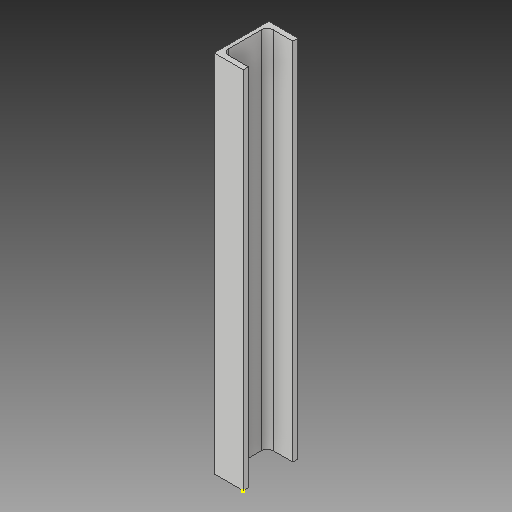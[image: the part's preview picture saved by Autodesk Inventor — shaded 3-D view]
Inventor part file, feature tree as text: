
AUTODESK INVENTOR PART (.ipt)
format: ipt  version: 2019 (Build 230136000, 136)  size: 93,184 bytes
history: native  units: in
note: dims shown in document units (in); Inventor stores cm internally (conversion verified against a paired STEP export)
features: other x3, sketch x2
ambient origin geometry x8: Origin, YZ Plane, XZ Plane, XY Plane, X Axis, Y Axis, Z Axis, Center Point
bodies: Solid1 (feature_tree)
feature tree (5):
  other  "Channel2_MIR1.ipt"
  other  "Solid1::Channel2_MIR1.ipt"
  other  "TaggingFeature1"
  sketch  "Sketch1"  dims[d0=0.3937in]
  sketch  "Sketch2"
